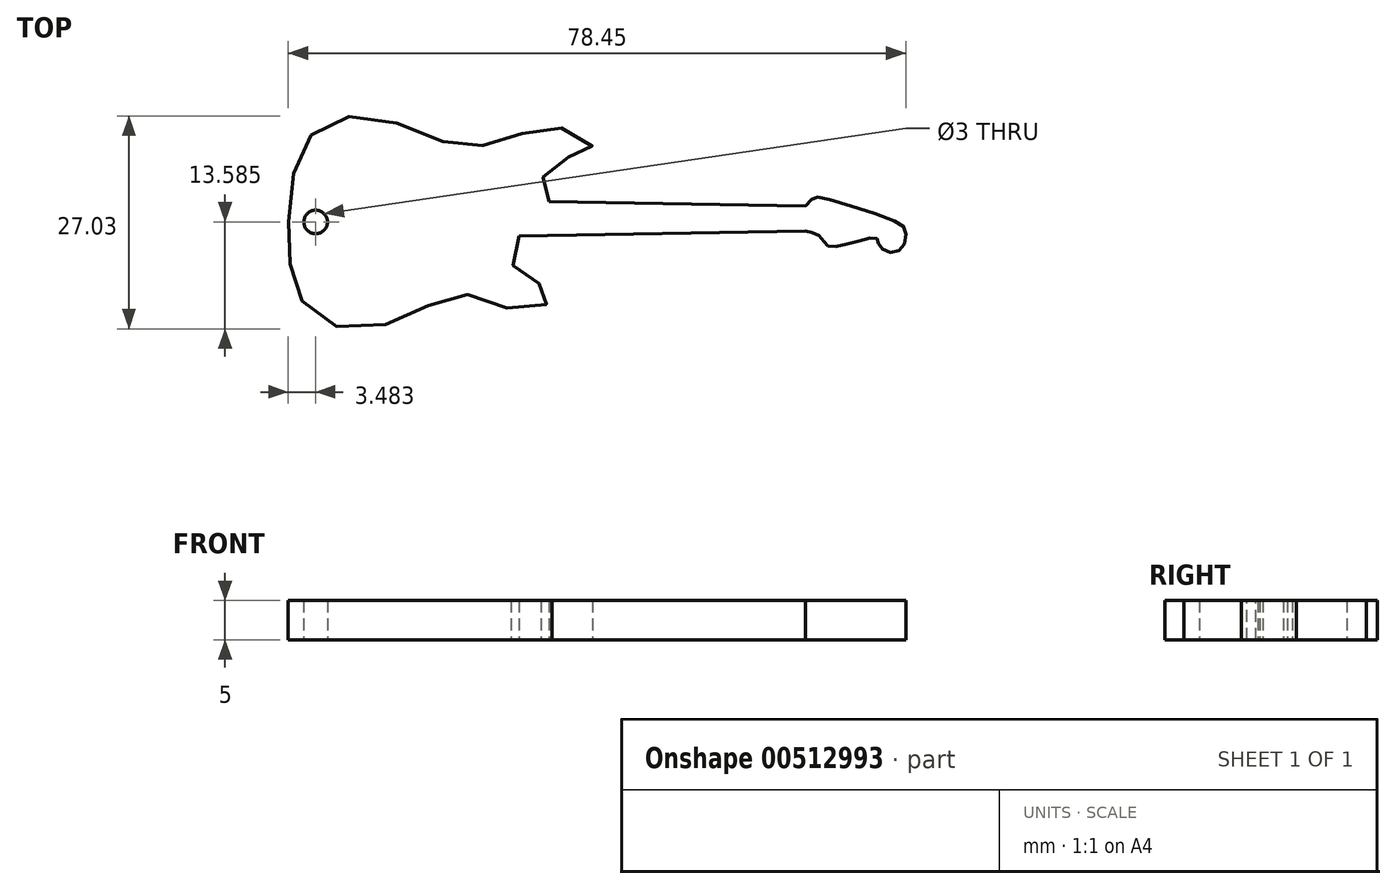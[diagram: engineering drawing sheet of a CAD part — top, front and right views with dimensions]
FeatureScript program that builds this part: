
annotation { "Feature Type Name" : "Feature", "Feature Type Description" : "" }
export const myFeature = defineFeature(function(context is Context, id is Id, definition is map)
    precondition{}
    {
        {
            var Q0;
            Q0=qCreatedBy(makeId("Top.planeOp"),FACE);
            var sketch = newSketch(context, id + "F0", { "sketchPlane" : qUnion([Q0])});
            skFitSpline(sketch, "E0", {"points": [v(54.1, 31.24) * mm, v(53.18, 32.17) * mm, v(53.14, 33.56) * mm, v(53.75, 35.17) * mm, v(55.29, 36.55) * mm, v(58.05, 36.93) * mm, v(59.27, 37.24) * mm, v(59.5, 38.62) * mm, v(57.74, 40.08) * mm, v(54.52, 40.62) * mm, v(51.68, 40.08) * mm, v(48.46, 39.31) * mm, v(45.47, 38.32) * mm, v(42.56, 38.32) * mm, v(39.33, 39.39) * mm, v(34.66, 41.23) * mm, v(30.2, 42.07) * mm, v(26.6, 41.54) * mm, v(23.84, 39.62) * mm, v(22.08, 36.17) * mm, v(21.39, 33.71) * mm, v(21.03, 28.75) * mm, v(20.99, 25.42) * mm, v(21.47, 21.98) * mm, v(22.23, 19.53) * mm, v(24.38, 16.69) * mm, v(27.6, 15.23) * mm, v(32.05, 15.3) * mm, v(36.73, 17) * mm, v(39.64, 18.45) * mm, v(42.79, 19.45) * mm, v(45.62, 18.84) * mm, v(48.84, 17.68) * mm, v(52.22, 17.6) * mm, v(54.21, 18.6) * mm, v(54.29, 20.14) * mm, v(52.68, 20.83) * mm, v(50.92, 21.37) * mm, v(49.53, 23.13) * mm, v(49.38, 24.97) * mm, v(50.22, 26.81) * mm, v(50.53, 26.81) * mm], "startDerivative": vector(-68.53, 43.45) * mm, "endDerivative": vector(35.6, -13.46) * mm});
            skLineSegment(sketch, "E1", {"start": v(54.1, 31.24) * mm, "end": v(86.65, 30.65) * mm});
            skLineSegment(sketch, "E2", {"start": v(86.65, 27.5) * mm, "end": v(50.3, 26.85) * mm});
            skFitSpline(sketch, "E3", {"points": [v(86.65, 30.65) * mm, v(87.73, 31.64) * mm, v(88.95, 31.64) * mm, v(98.23, 28.65) * mm, v(99.3, 27.65) * mm, v(99.23, 25.81) * mm, v(98.08, 24.82) * mm, v(96.62, 25.05) * mm, v(95.93, 25.9) * mm, v(95.78, 26.5) * mm, v(94.94, 26.58) * mm, v(92.33, 25.9) * mm, v(89.95, 25.5) * mm, v(89.26, 25.81) * mm, v(88.65, 26.66) * mm, v(87.57, 27.27) * mm, v(86.65, 27.5) * mm], "startDerivative": vector(19.02, 20.45) * mm, "endDerivative": vector(-18.6, 3.74) * mm});
            skPoint(sketch, "E4.0.internal.orphan", {"position": v(48.38, 26.81) * mm});
            skCircle(sketch, "E5", {"center": v(24.44, 28.63) * mm, "radius": 1.5 * mm});
            skSolve(sketch);
        }
        {
            var Q0;
            Q0 = qSketchRegion(id + "F0", true);
            extrude(context, id + "F1", {"entities" : qUnion([Q0]), "depth" : 5 * mm});
        }
    });
